# Revit family: Apollo Triple
name_source: partatom
category: Lighting Fixtures
revit_build: Autodesk Revit 2018 (Build: 20170223_1515(x64)
units: mm (PartAtom-declared; Revit-internal decimal feet)

## family parameters
Always vertical = Yes
Cut with Voids When Loaded = No
Host = Ceiling
Light Source = No
OmniClass Number = 23.80.70.11
OmniClass Title = Luminaries for Internal Lighting
Part Type = Normal
Room Calculation Point = No
Round Connector Dimension = Use Diameter
Shared = No

## types (1)
- CE
    ADA compliant = Not Applicable
    Dimmable = Yes
    Dimming Method = Lamp dependent
    Driver Included = Not Applicable
    Driver Required = No
    Efficacy (lm/w) = Lamp dependent
    Electrical Class = 1
    Lamp = Gu10
    Light Source Fixed = No
    Location / IP Rating = IP20
    Main Finish = Various
    Main Material = Metal - aluminium
    Manufacturer URL - Europe and Rest of World = www.astrolighting.com
    Manufacturer URL - North America = us.astrolighting.com
    Product CCT = Lamp dependent
    Product CRI = Lamp dependent
    Product Location = Indoor
    Product Name = Apollo triple bar
    Product SKU = 1422008
    Product Weight (KG) = 0 mm  [stored 0 ft]

note: [stored X ft] marks values corroborated as IEEE doubles in the binary element streams (Revit-internal decimal feet)

## geometry (parser evidence)
native form markers: Sweep x2
no freeform markers — native parametric forms only
